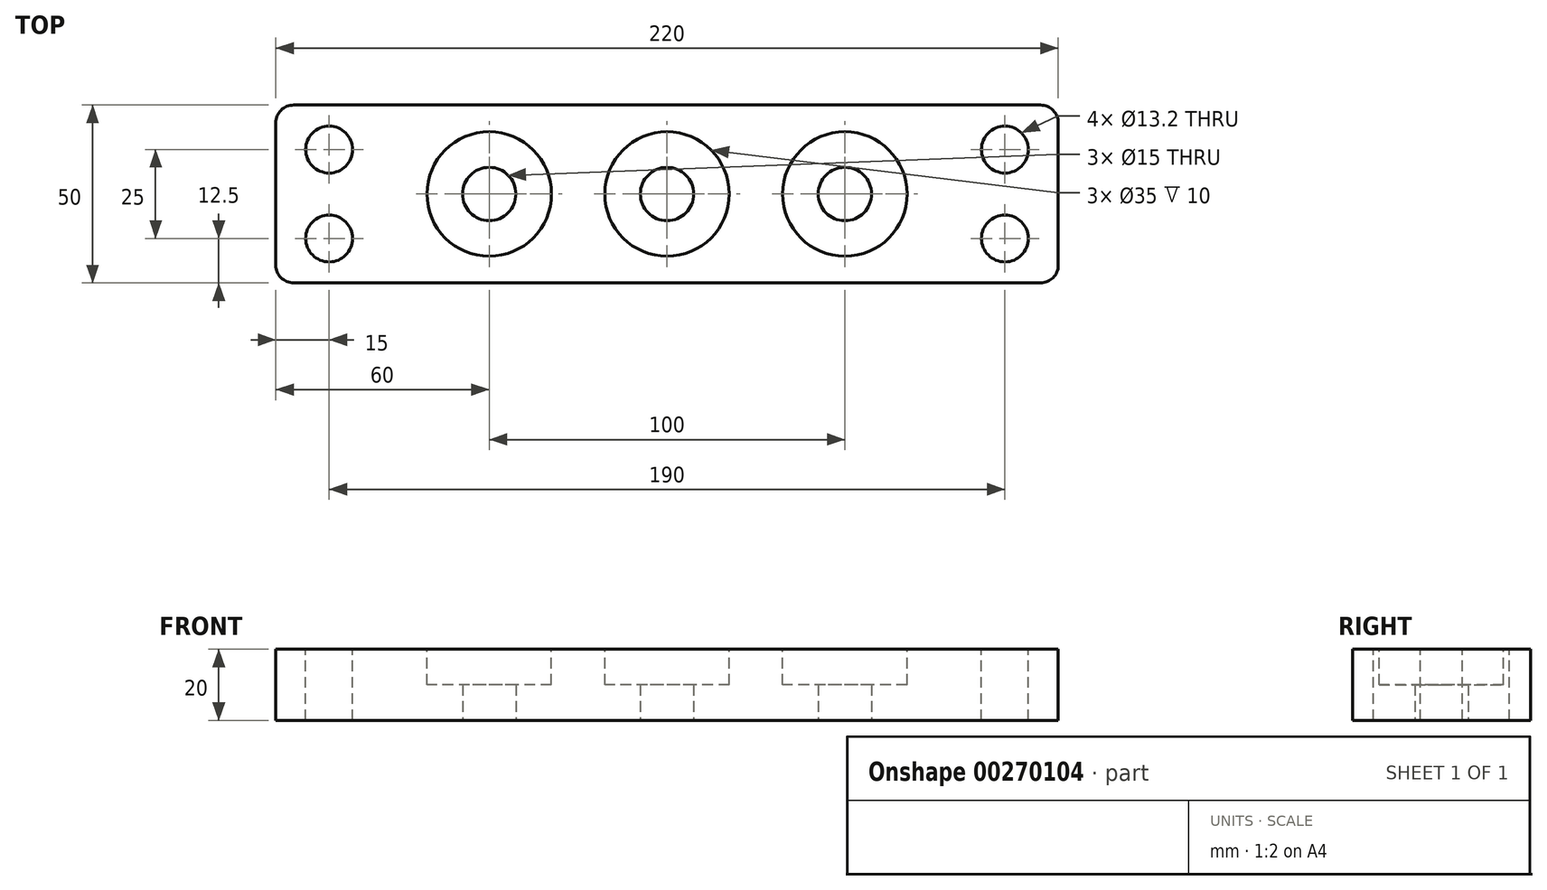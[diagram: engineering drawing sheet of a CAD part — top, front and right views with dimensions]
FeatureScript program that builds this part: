
annotation { "Feature Type Name" : "Feature", "Feature Type Description" : "" }
export const myFeature = defineFeature(function(context is Context, id is Id, definition is map)
    precondition{}
    {
        {
            var Q0;
            Q0=qCreatedBy(makeId("Top.planeOp"),FACE);
            var sketch = newSketch(context, id + "F0", { "sketchPlane" : qUnion([Q0])});
            skLineSegment(sketch, "E0.bottom", {"start": v(110, -25) * mm, "end": v(-110, -25) * mm});
            skLineSegment(sketch, "E0.top", {"start": v(110, 25) * mm, "end": v(-110, 25) * mm});
            skLineSegment(sketch, "E0.left", {"start": v(110, -25) * mm, "end": v(110, 25) * mm});
            skLineSegment(sketch, "E0.right", {"start": v(-110, -25) * mm, "end": v(-110, 25) * mm});
            skPoint(sketch, "E0.middle", {"position": v(0, 0) * mm});
            skPoint(sketch, "E1", {"position": v(-50, 0) * mm});
            skPoint(sketch, "E2", {"position": v(50, 0) * mm});
            skCircle(sketch, "E3", {"center": v(50, 0) * mm, "radius": 7.5 * mm});
            skCircle(sketch, "E4", {"center": v(-50, 0) * mm, "radius": 7.5 * mm});
            skCircle(sketch, "E5", {"center": v(0, 0) * mm, "radius": 7.5 * mm});
            skPoint(sketch, "E6", {"position": v(-95, 12.5) * mm});
            skPoint(sketch, "E7", {"position": v(-95, -12.5) * mm});
            skPoint(sketch, "E8", {"position": v(95, 12.5) * mm});
            skPoint(sketch, "E9", {"position": v(95, -12.5) * mm});
            skSolve(sketch);
        }
        {
            var Q0;
            Q0=makeQuery(id+"F0.imprint","IMPRINT",FACE,{"disambiguationData":[TD([[makeQuery(id+"F0.imprint","IMPRINT",EDGE,{"derivedFrom":sQuery(id+"F0.wireOp",EDGE,"E0.bottom")}),-1.0]])]});
            extrude(context, id + "F1", {"entities" : qUnion([Q0]), "depth" : 20 * mm});
        }
        {
            var Q0;
            Q0=sQuery(id+"F0.wireOp",VERTEX,"E6");
            var Q1;
            Q1=sQuery(id+"F0.wireOp",VERTEX,"E7");
            var Q2;
            Q2=sQuery(id+"F0.wireOp",VERTEX,"E8");
            var Q3;
            Q3=sQuery(id+"F0.wireOp",VERTEX,"E9");
            var Q4;
            Q4=makeQuery(id+"F1.opExtrude","SWEPT_BODY",BODY,{"disambiguationData":[OSD([sQuery(id+"F0.wireOp",EDGE,"E0.bottom"),sQuery(id+"F0.wireOp",EDGE,"E0.top"),sQuery(id+"F0.wireOp",EDGE,"E0.left"),sQuery(id+"F0.wireOp",EDGE,"E0.right"),sQuery(id+"F0.wireOp",EDGE,"E3"),sQuery(id+"F0.wireOp",EDGE,"E4"),sQuery(id+"F0.wireOp",EDGE,"E5")])]});
            hole(context, id + "F2", {"style" : HoleStyle.SIMPLE, "endStyle" : HoleEndStyle.THROUGH, "oppositeDirection" : true, "standardTappedOrClearance" : lookupTablePath({ "standard" : "ISO", "fit" : "Normal", "size" : "M12", "type" : "Clearance" }), "standardBlindInLast" : lookupTablePath({ "fit" : "Standard", "standard" : "ISO", "size" : "M12", "type" : "Clearance" }), "holeDiameter" : 13.2 * mm, "tappedDepth" : 60 * mm, "tapClearance" : 3, "startFromSketch" : true, "locations" : qUnion([Q0, Q1, Q2, Q3]), "scope" : qUnion([Q4])});
        }
        {
            var Q0;
            Q0=makeQuery(id+"F1.opExtrude","SWEPT_EDGE",EDGE,{"disambiguationData":[OSD([sQuery(id+"F0.wireOp",EDGE,"E0.bottom"),sQuery(id+"F0.wireOp",EDGE,"E0.right")])]});
            var Q1;
            Q1=makeQuery(id+"F1.opExtrude","SWEPT_EDGE",EDGE,{"disambiguationData":[OSD([sQuery(id+"F0.wireOp",EDGE,"E0.bottom"),sQuery(id+"F0.wireOp",EDGE,"E0.left")])]});
            var Q2;
            Q2=makeQuery(id+"F1.opExtrude","SWEPT_EDGE",EDGE,{"disambiguationData":[OSD([sQuery(id+"F0.wireOp",EDGE,"E0.top"),sQuery(id+"F0.wireOp",EDGE,"E0.left")])]});
            var Q3;
            Q3=makeQuery(id+"F1.opExtrude","SWEPT_EDGE",EDGE,{"disambiguationData":[OSD([sQuery(id+"F0.wireOp",EDGE,"E0.top"),sQuery(id+"F0.wireOp",EDGE,"E0.right")])]});
            fillet(context, id + "F3", {"entities" : qUnion([Q0, Q1, Q2, Q3]), "radius" : 5 * mm, "tangentPropagation" : true, "allowEdgeOverflow" : false});
        }
        {
            var Q0;
            Q0=makeQuery(id+"F1.opExtrude","CAP_FACE",FACE,{"disambiguationData":[OSD([sQuery(id+"F0.wireOp",EDGE,"E0.bottom"),sQuery(id+"F0.wireOp",EDGE,"E0.top"),sQuery(id+"F0.wireOp",EDGE,"E0.left"),sQuery(id+"F0.wireOp",EDGE,"E0.right"),sQuery(id+"F0.wireOp",EDGE,"E3"),sQuery(id+"F0.wireOp",EDGE,"E4"),sQuery(id+"F0.wireOp",EDGE,"E5")])],"isStart":false});
            var sketch = newSketch(context, id + "F4", { "sketchPlane" : qUnion([Q0])});
            skCircle(sketch, "E10", {"center": v(-50, 0) * mm, "radius": 17.5 * mm});
            skCircle(sketch, "E11", {"center": v(50, 0) * mm, "radius": 17.5 * mm});
            skCircle(sketch, "E12", {"center": v(0, 0) * mm, "radius": 17.5 * mm});
            skSolve(sketch);
        }
        {
            var Q0;
            Q0=makeQuery(id+"F4.imprint","IMPRINT",FACE,{"disambiguationData":[TD([[makeQuery(id+"F4.imprint","IMPRINT",EDGE,{"derivedFrom":sQuery(id+"F4.wireOp",EDGE,"E10")}),1.0]])]});
            var Q1;
            Q1=makeQuery(id+"F4.imprint","IMPRINT",FACE,{"disambiguationData":[TD([[makeQuery(id+"F4.imprint","IMPRINT",EDGE,{"derivedFrom":sQuery(id+"F4.wireOp",EDGE,"E11")}),1.0]])]});
            var Q2;
            Q2=makeQuery(id+"F4.imprint","IMPRINT",FACE,{"disambiguationData":[TD([[makeQuery(id+"F4.imprint","IMPRINT",EDGE,{"derivedFrom":sQuery(id+"F4.wireOp",EDGE,"E12")}),1.0]])]});
            extrude(context, id + "F5", {"entities" : qUnion([Q0, Q1, Q2]), "operationType" : NewBodyOperationType.REMOVE, "oppositeDirection" : true, "depth" : 10 * mm});
        }
    });
